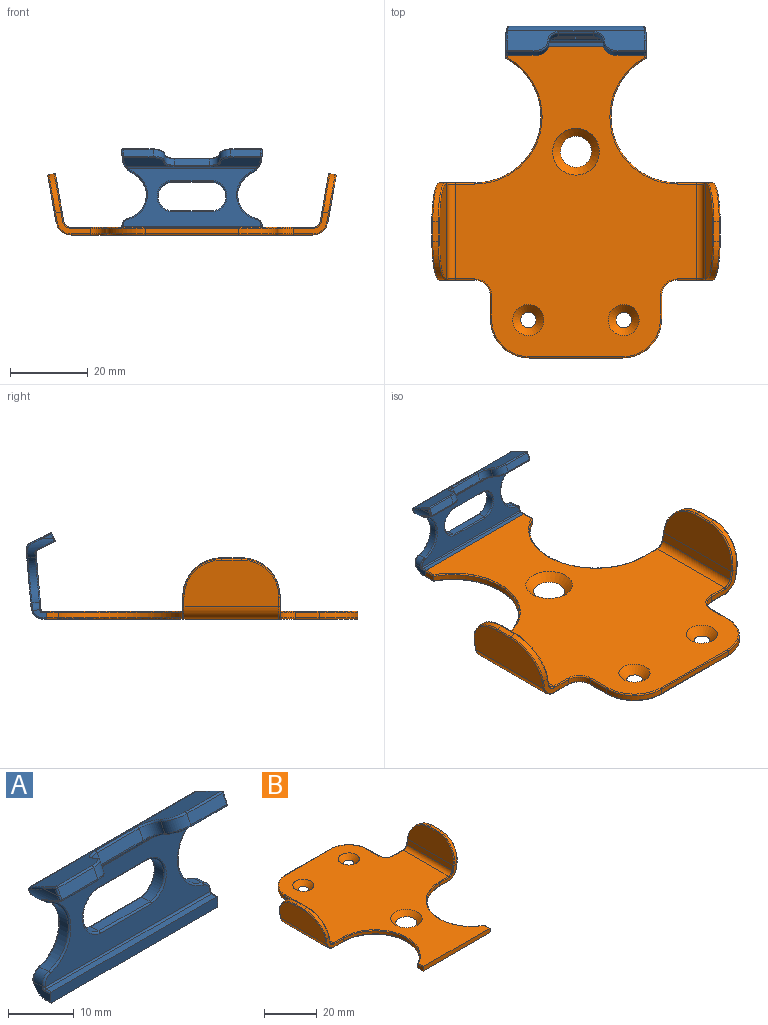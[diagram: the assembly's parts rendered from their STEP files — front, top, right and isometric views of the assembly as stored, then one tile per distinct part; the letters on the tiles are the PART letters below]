
ASSEMBLY  parts=2 mates=1
PART A: 99 faces, bbox 36.3x7.8x22.5 mm
  f0: plane 35.22x14.86mm, normal (0,1,-0.09), area 265.9mm2, adj f8,f15,f29,f30,f31,f32,f52,f53
  f1: plane 3.57x2.09mm, normal (1,0,0), area 4.9mm2, adj f6,f35,f46,f47,f48,f56,f57
  f2: plane 3.57x2.09mm, normal (-1,0,0), area 4.9mm2, adj f6,f36,f58,f59,f72,f73,f74
  f3: plane 11.89x4.49mm, normal (0,-0.45,-0.89), area 50.1mm2, adj f16,f41,f84,f86,f88
  f4: plane 35.4x5.1mm, normal (0,0.45,0.89), area 124.1mm2, adj f8,f49,f50,f65,f66,f87,f89,f91
  f5: plane 7.7x1.7mm, normal (0,-0.89,0.45), area 14.6mm2, adj f39,f77,f81,f83,f87
  f6: plane 36x2mm, normal (0,-1,0), area 71.9mm2, adj f1,f2,f7,f12,f48,f57,f58,f74
  f7: plane 35.4x0.98mm, normal (0,0,-1), area 34.8mm2, adj f6,f15,f57,f58
  f8: cylinder r=2mm len=35.17mm, axis (-1,0,0), area 82.8mm2, adj f0,f4,f51,f64
  f9: plane 7.7x1.7mm, normal (0,-0.89,0.45), area 14.6mm2, adj f40,f88,f92,f94,f98
  f10: plane 11.89x4.49mm, normal (0,-0.45,-0.89), area 50.1mm2, adj f16,f67,f75,f76,f77
  f11: plane 35.4x14.87mm, normal (0,-1,0.09), area 267.4mm2, adj f16,f17,f25,f26,f27,f28,f43,f44
  f12: plane 35.4x1.12mm, normal (0,0,1), area 39.7mm2, adj f6,f17,f48,f74
  f13: plane 3.08x1.29mm, normal (1,0,0), area 1.6mm2, adj f33,f49,f94
  f14: plane 3.08x1.29mm, normal (-1,0,0), area 1.6mm2, adj f34,f66,f83
  f15: cylinder r=3mm len=35.4mm, axis (-1,0,0), area 157.5mm2, adj f0,f7,f55,f56,f59,f60
  f16: cylinder r=0.5mm len=33.89mm, axis (1,0,0), area 17.9mm2, adj f3,f10,f11,f42,f68,f78,f80,f82
  f17: cylinder r=0.3mm len=35.4mm, axis (1,0,0), area 15.8mm2, adj f11,f12,f47,f73
  f18: plane 9x1.75mm, normal (0,-0.89,0.45), area 17.6mm2, adj f37,f38,f80,f93
  f19: cylinder r=6.25mm len=11.78mm, axis (0,1,-0.09), area 28.9mm2, adj f34,f36,f62,f70
  f20: cylinder r=6.25mm len=11.78mm, axis (0,1,-0.09), area 28.9mm2, adj f33,f35,f44,f53
  f21: plane 11x1.89mm, normal (0,-0.09,-1), area 20.9mm2, adj f22,f24,f28,f29
  f22: cylinder r=3.8mm len=7.64mm, axis (0,1,-0.09), area 20.3mm2, adj f21,f23,f27,f31
  f23: plane 11x1.89mm, normal (0,0.09,1), area 20.9mm2, adj f22,f24,f25,f32
  f24: cylinder r=3.8mm len=7.64mm, axis (0,1,-0.09), area 20.3mm2, adj f21,f23,f26,f30
  f25: cylinder r=0.3mm len=11.05mm, axis (-1,0,0), area 5.2mm2, adj f11,f23,f26,f27
  f26: torus R=4.1mm, axis (0,1,-0.09), area 5.2mm2, adj f11,f24,f25,f28
  f27: torus R=4.1mm, axis (0,1,-0.09), area 5.2mm2, adj f11,f22,f25,f28
  f28: cylinder r=0.3mm len=11.05mm, axis (1,0,0), area 5.2mm2, adj f11,f21,f26,f27
  f29: cylinder r=0.3mm len=11.05mm, axis (1,0,0), area 5.2mm2, adj f0,f21,f30,f31
  f30: torus R=4.1mm, axis (0,-1,0.09), area 5.2mm2, adj f0,f24,f29,f32
  f31: torus R=4.1mm, axis (0,-1,0.09), area 5.2mm2, adj f0,f22,f29,f32
  f32: cylinder r=0.3mm len=11.05mm, axis (-1,0,0), area 5.2mm2, adj f0,f23,f30,f31
  f33: cylinder r=5mm len=7.44mm, axis (0,1,-0.09), area 17.3mm2, adj f13,f20,f41,f42,f43,f50,f51,f52
  f34: cylinder r=5mm len=7.44mm, axis (0,1,-0.09), area 17.3mm2, adj f14,f19,f63,f64,f65,f67,f68,f69
  f35: cylinder r=2mm len=2.1mm, axis (0,1,-0.09), area 5mm2, adj f1,f20,f45,f54,f55
  f36: cylinder r=2mm len=2.1mm, axis (0,1,-0.09), area 5mm2, adj f2,f19,f60,f61,f71
  f37: cylinder r=2.5mm len=3.04mm, axis (0,0.45,0.89), area 7.3mm2, adj f18,f40,f82,f84,f95
  f38: cylinder r=2.5mm len=3.04mm, axis (0,-0.45,-0.89), area 7.3mm2, adj f18,f39,f76,f78,f91
  f39: cylinder r=3mm len=3.45mm, axis (0,-0.45,-0.89), area 8.8mm2, adj f5,f38,f75,f89
  f40: cylinder r=3mm len=3.45mm, axis (0,0.45,0.89), area 8.8mm2, adj f9,f37,f86,f97
  f41: bspline ~4.61x2.47mm, area 1.9mm2, adj f3,f33,f42,f90
  f42: bspline ~1.15x1.14mm, area 0.4mm2, adj f16,f33,f41,f43
  f43: torus R=4.7mm, axis (0,1,-0.09), area 0.8mm2, adj f11,f33,f42,f44
  f44: torus R=6.55mm, axis (0,1,-0.09), area 7.3mm2, adj f11,f20,f43,f45
  f45: torus R=1.7mm, axis (0,1,-0.09), area 1.2mm2, adj f11,f35,f44,f46
  f46: cylinder r=0.3mm len=0.31mm, axis (0,0.09,1), area 0.1mm2, adj f1,f11,f45,f47
  f47: torus R=0.6mm, axis (1,0,0), area 0.3mm2, adj f1,f17,f46,f48
  f48: cylinder r=0.3mm len=1.12mm, axis (0,1,0), area 0.5mm2, adj f1,f6,f12,f47
  f49: cylinder r=0.3mm len=2.71mm, axis (0,0.89,-0.45), area 1.4mm2, adj f4,f13,f50,f96
  f50: bspline ~4.11x2.33mm, area 1.4mm2, adj f4,f33,f49,f51
  f51: bspline ~2.43x1.6mm, area 1.3mm2, adj f8,f33,f50,f52
  f52: torus R=4.7mm, axis (0,-1,0.09), area 1.2mm2, adj f0,f33,f51,f53
  f53: torus R=6.55mm, axis (0,-1,0.09), area 7.3mm2, adj f0,f20,f52,f54
  f54: torus R=1.7mm, axis (0,-1,0.09), area 0.9mm2, adj f0,f35,f53,f55
  f55: bspline ~1.55x0.55mm, area 0.3mm2, adj f15,f35,f54,f56
  f56: torus R=2.7mm, axis (1,0,0), area 1.7mm2, adj f1,f15,f55,f57
  f57: cylinder r=0.3mm len=0.98mm, axis (0,-1,0), area 0.5mm2, adj f1,f6,f7,f56
  f58: cylinder r=0.3mm len=0.98mm, axis (0,1,0), area 0.5mm2, adj f2,f6,f7,f59
  f59: torus R=2.7mm, axis (1,0,0), area 1.7mm2, adj f2,f15,f58,f60
  f60: bspline ~1.55x0.55mm, area 0.3mm2, adj f15,f36,f59,f61
  f61: torus R=1.7mm, axis (0,-1,0.09), area 0.9mm2, adj f0,f36,f60,f62
  f62: torus R=6.55mm, axis (0,-1,0.09), area 7.3mm2, adj f0,f19,f61,f63
  f63: torus R=4.7mm, axis (0,-1,0.09), area 1.2mm2, adj f0,f34,f62,f64
  f64: bspline ~2.7x1.4mm, area 1.3mm2, adj f8,f34,f63,f65
  f65: bspline ~4.11x2.33mm, area 1.4mm2, adj f4,f34,f64,f66
  f66: cylinder r=0.3mm len=2.71mm, axis (0,-0.89,0.45), area 1.4mm2, adj f4,f14,f65,f85
  f67: bspline ~4.61x2.47mm, area 1.9mm2, adj f10,f34,f68,f79
  f68: bspline ~1.12x1.11mm, area 0.4mm2, adj f16,f34,f67,f69
  f69: torus R=4.7mm, axis (0,1,-0.09), area 0.8mm2, adj f11,f34,f68,f70
  f70: torus R=6.55mm, axis (0,1,-0.09), area 7.3mm2, adj f11,f19,f69,f71
  f71: torus R=1.7mm, axis (0,1,-0.09), area 1.2mm2, adj f11,f36,f70,f72
  f72: cylinder r=0.3mm len=0.31mm, axis (0,-0.09,-1), area 0.1mm2, adj f2,f11,f71,f73
  f73: torus R=0.6mm, axis (1,0,0), area 0.3mm2, adj f2,f17,f72,f74
  f74: cylinder r=0.3mm len=1.12mm, axis (0,-1,0), area 0.5mm2, adj f2,f6,f12,f73
  f75: torus R=2.7mm, axis (0,0.45,0.89), area 2.1mm2, adj f10,f39,f76,f77
  f76: torus R=2.8mm, axis (0,0.45,0.89), area 1.3mm2, adj f10,f38,f75,f78
  f77: cylinder r=0.3mm len=7.65mm, axis (-1,0,0), area 3.6mm2, adj f5,f10,f75,f79
  f78: bspline ~1.76x0.52mm, area 0.5mm2, adj f16,f38,f76,f80
  f79: sphere r=0.3mm, area 0.1mm2, adj f67,f77,f81
  f80: cylinder r=0.3mm len=9mm, axis (1,0,0), area 3.2mm2, adj f16,f18,f78,f82
  f81: bspline ~1.79x1.09mm, area 0.4mm2, adj f5,f34,f79,f83
  f82: bspline ~2.03x0.55mm, area 0.5mm2, adj f16,f37,f80,f84
  f83: cylinder r=0.3mm len=1.15mm, axis (0,-0.45,-0.89), area 0.5mm2, adj f5,f14,f81,f85
  f84: torus R=2.8mm, axis (0,0.45,0.89), area 1.3mm2, adj f3,f37,f82,f86
  f85: sphere r=0.3mm, area 0.1mm2, adj f66,f83,f87
  f86: torus R=2.7mm, axis (0,0.45,0.89), area 2.1mm2, adj f3,f40,f84,f88
  f87: cylinder r=0.3mm len=7.7mm, axis (-1,0,0), area 3.6mm2, adj f4,f5,f85,f89
  f88: cylinder r=0.3mm len=7.65mm, axis (-1,0,0), area 3.6mm2, adj f3,f9,f86,f90
  f89: torus R=2.7mm, axis (0,-0.45,-0.89), area 2.1mm2, adj f4,f39,f87,f91
  f90: sphere r=0.3mm, area 0.1mm2, adj f41,f88,f92
  f91: torus R=2.8mm, axis (0,-0.45,-0.89), area 1.9mm2, adj f4,f38,f89,f93
  f92: bspline ~1.79x1.09mm, area 0.4mm2, adj f9,f33,f90,f94
  f93: cylinder r=0.3mm len=9mm, axis (1,0,0), area 4.2mm2, adj f4,f18,f91,f95
  f94: cylinder r=0.3mm len=1.15mm, axis (0,0.45,0.89), area 0.5mm2, adj f9,f13,f92,f96
  f95: torus R=2.8mm, axis (0,-0.45,-0.89), area 1.9mm2, adj f4,f37,f93,f97
  f96: sphere r=0.3mm, area 0.1mm2, adj f49,f94,f98
  f97: torus R=2.7mm, axis (0,-0.45,-0.89), area 2.1mm2, adj f4,f40,f95,f98
  f98: cylinder r=0.3mm len=7.7mm, axis (-1,0,0), area 3.6mm2, adj f4,f9,f96,f97
PART B: 94 faces, bbox 74.4x80.9x17 mm
  f0: plane 24x1.4mm, normal (0,1,0), area 33.6mm2, adj f1,f15,f64,f82
  f1: cylinder r=10mm len=10mm, axis (0,0,-1), area 22mm2, adj f0,f2,f62,f80
  f2: plane 6x1.4mm, normal (-1,0,0), area 8.4mm2, adj f1,f3,f60,f78
  f3: cylinder r=4mm len=4mm, axis (0,0,-1), area 8.8mm2, adj f2,f4,f58,f76
  f4: plane 9.05x5.62mm, normal (0,1,0), area 16.2mm2, adj f3,f23,f52,f54,f56,f73,f74,f75
  f5: plane 9.05x5.62mm, normal (0,-1,0), area 16.2mm2, adj f6,f24,f40,f42,f44,f67,f68,f69
  f6: cylinder r=17mm len=32mm, axis (0,0,-1), area 63.1mm2, adj f5,f7,f38,f66
  f7: plane 3.06x1.76mm, normal (-1,0,0), area 5.1mm2, adj f6,f8,f17,f38,f65
  f8: plane 36x2mm, normal (0,-1,0), area 71.9mm2, adj f7,f9,f16,f17,f37,f65,f77
  f9: plane 3x1.4mm, normal (1,0,0), area 4.2mm2, adj f8,f10,f37,f77
  f10: cylinder r=17mm len=32mm, axis (0,0,-1), area 63.1mm2, adj f9,f11,f39,f79
  f11: plane 9.05x5.62mm, normal (0,-1,0), area 16.2mm2, adj f10,f32,f41,f43,f45,f81,f83,f85
  f12: plane 9.05x5.62mm, normal (0,1,0), area 16.2mm2, adj f13,f31,f53,f55,f57,f90,f92,f93
  f13: cylinder r=4mm len=4mm, axis (0,0,-1), area 8.8mm2, adj f12,f14,f59,f88
  f14: plane 6x1.4mm, normal (1,0,0), area 8.4mm2, adj f13,f15,f61,f86
  f15: cylinder r=10mm len=10mm, axis (0,0,-1), area 22mm2, adj f0,f14,f63,f84
  f16: plane 79.7x62mm, normal (0,0,1), area 3007mm2, adj f8,f18,f26,f34,f35,f36,f65,f66
  f17: plane 79.7x62mm, normal (0,0,-1), area 3146.1mm2, adj f7,f8,f21,f29,f34,f35,f36,f37
  f18: cylinder r=2mm len=24.4mm, axis (0,-1,0), area 68.1mm2, adj f16,f19,f68,f74
  f19: plane 24.4x2.32mm, normal (0.98,0,0.17), area 57.4mm2, adj f18,f25,f69,f73
  f20: plane 24.4x11.87mm, normal (-0.98,0,-0.17), area 253.7mm2, adj f21,f44,f46,f48,f50,f52
  f21: cylinder r=4mm len=24.4mm, axis (0,-1,0), area 136.3mm2, adj f17,f20,f42,f54
  f22: plane 5x1.38mm, normal (-0.17,0,0.98), area 7mm2, adj f23,f24,f48,f71
  f23: cylinder r=10mm len=10.09mm, axis (-0.98,0,-0.17), area 22mm2, adj f4,f22,f50,f72
  f24: cylinder r=10mm len=10.09mm, axis (-0.98,0,-0.17), area 22mm2, adj f5,f22,f46,f70
  f25: plane 24.4x9.55mm, normal (0.98,0,0.17), area 196.3mm2, adj f19,f70,f71,f72
  f26: cylinder r=2mm len=24.4mm, axis (0,-1,0), area 68.1mm2, adj f16,f27,f83,f92
  f27: plane 24.4x2.32mm, normal (-0.98,0,0.17), area 57.4mm2, adj f26,f33,f85,f93
  f28: plane 24.4x11.87mm, normal (0.98,0,-0.17), area 253.7mm2, adj f29,f45,f47,f49,f51,f53
  f29: cylinder r=4mm len=24.4mm, axis (0,-1,0), area 136.3mm2, adj f17,f28,f43,f55
  f30: plane 5x1.38mm, normal (0.17,0,0.98), area 7mm2, adj f31,f32,f49,f89
  f31: cylinder r=10mm len=10.09mm, axis (0.98,0,-0.17), area 22mm2, adj f12,f30,f51,f91
  f32: cylinder r=10mm len=10.09mm, axis (0.98,0,-0.17), area 22mm2, adj f11,f30,f47,f87
  f33: plane 24.4x9.55mm, normal (-0.98,0,0.17), area 196.3mm2, adj f27,f87,f89,f91
  f34: cone r=2mm half-angle=45deg, axis (0,0,1), area 53.3mm2, adj f16,f17
  f35: cone r=2mm half-angle=45deg, axis (0,0,1), area 53.3mm2, adj f16,f17
  f36: cone r=4mm half-angle=45deg, axis (0,0,1), area 88.9mm2, adj f16,f17
  f37: cylinder r=0.3mm len=3mm, axis (0,1,0), area 1.4mm2, adj f8,f9,f17,f39
  f38: torus R=17.3mm, axis (0,0,1), area 21.4mm2, adj f6,f7,f17,f40
  f39: torus R=17.3mm, axis (0,0,1), area 21.3mm2, adj f10,f17,f37,f41
  f40: cylinder r=0.3mm len=5mm, axis (1,0,0), area 2.4mm2, adj f5,f17,f38,f42
  f41: cylinder r=0.3mm len=5mm, axis (1,0,0), area 2.4mm2, adj f11,f17,f39,f43
  f42: torus R=3.7mm, axis (0,1,0), area 2.6mm2, adj f5,f21,f40,f44
  f43: torus R=3.7mm, axis (0,-1,0), area 2.6mm2, adj f11,f29,f41,f45
  f44: cylinder r=0.3mm len=2.37mm, axis (-0.17,0,0.98), area 1.1mm2, adj f5,f20,f42,f46
  f45: cylinder r=0.3mm len=2.37mm, axis (-0.17,0,-0.98), area 1.1mm2, adj f11,f28,f43,f47
  f46: torus R=9.7mm, axis (0.98,0,0.17), area 7.3mm2, adj f20,f24,f44,f48
  f47: torus R=9.7mm, axis (-0.98,0,0.17), area 7.3mm2, adj f28,f32,f45,f49
  f48: cylinder r=0.3mm len=5mm, axis (0,-1,0), area 2.4mm2, adj f20,f22,f46,f50
  f49: cylinder r=0.3mm len=5mm, axis (0,-1,0), area 2.4mm2, adj f28,f30,f47,f51
  f50: torus R=9.7mm, axis (0.98,0,0.17), area 7.3mm2, adj f20,f23,f48,f52
  f51: torus R=9.7mm, axis (-0.98,0,0.17), area 7.3mm2, adj f28,f31,f49,f53
  f52: cylinder r=0.3mm len=2.37mm, axis (-0.17,0,0.98), area 1.1mm2, adj f4,f20,f50,f54
  f53: cylinder r=0.3mm len=2.37mm, axis (-0.17,0,-0.98), area 1.1mm2, adj f12,f28,f51,f55
  f54: torus R=3.7mm, axis (0,-1,0), area 2.6mm2, adj f4,f21,f52,f56
  f55: torus R=3.7mm, axis (0,1,0), area 2.6mm2, adj f12,f29,f53,f57
  f56: cylinder r=0.3mm len=5mm, axis (-1,0,0), area 2.4mm2, adj f4,f17,f54,f58
  f57: cylinder r=0.3mm len=5mm, axis (-1,0,0), area 2.4mm2, adj f12,f17,f55,f59
  f58: torus R=4.3mm, axis (0,0,1), area 3mm2, adj f3,f17,f56,f60
  f59: torus R=4.3mm, axis (0,0,1), area 3mm2, adj f13,f17,f57,f61
  f60: cylinder r=0.3mm len=6mm, axis (0,-1,0), area 2.8mm2, adj f2,f17,f58,f62
  f61: cylinder r=0.3mm len=6mm, axis (0,1,0), area 2.8mm2, adj f14,f17,f59,f63
  f62: torus R=9.7mm, axis (0,0,1), area 7.3mm2, adj f1,f17,f60,f64
  f63: torus R=9.7mm, axis (0,0,1), area 7.3mm2, adj f15,f17,f61,f64
  f64: cylinder r=0.3mm len=24mm, axis (-1,0,0), area 11.3mm2, adj f0,f17,f62,f63
  f65: cylinder r=0.3mm len=3mm, axis (0,1,0), area 1.4mm2, adj f7,f8,f16,f66
  f66: torus R=17.3mm, axis (0,0,1), area 21.3mm2, adj f6,f16,f65,f67
  f67: cylinder r=0.3mm len=5mm, axis (-1,0,0), area 2.4mm2, adj f5,f16,f66,f68
  f68: torus R=2.3mm, axis (0,1,0), area 1.4mm2, adj f5,f18,f67,f69
  f69: cylinder r=0.3mm len=2.37mm, axis (0.17,0,-0.98), area 1.1mm2, adj f5,f19,f68,f70
  f70: torus R=9.7mm, axis (-0.98,0,-0.17), area 7.3mm2, adj f24,f25,f69,f71
  f71: cylinder r=0.3mm len=5mm, axis (0,-1,0), area 2.4mm2, adj f22,f25,f70,f72
  f72: torus R=9.7mm, axis (-0.98,0,-0.17), area 7.3mm2, adj f23,f25,f71,f73
  f73: cylinder r=0.3mm len=2.37mm, axis (0.17,0,-0.98), area 1.1mm2, adj f4,f19,f72,f74
  f74: torus R=2.3mm, axis (0,-1,0), area 1.4mm2, adj f4,f18,f73,f75
  f75: cylinder r=0.3mm len=5mm, axis (1,0,0), area 2.4mm2, adj f4,f16,f74,f76
  f76: torus R=4.3mm, axis (0,0,1), area 3mm2, adj f3,f16,f75,f78
  f77: cylinder r=0.3mm len=3mm, axis (0,-1,0), area 1.4mm2, adj f8,f9,f16,f79
  f78: cylinder r=0.3mm len=6mm, axis (0,1,0), area 2.8mm2, adj f2,f16,f76,f80
  f79: torus R=17.3mm, axis (0,0,1), area 21.3mm2, adj f10,f16,f77,f81
  f80: torus R=9.7mm, axis (0,0,1), area 7.3mm2, adj f1,f16,f78,f82
  f81: cylinder r=0.3mm len=5mm, axis (-1,0,0), area 2.4mm2, adj f11,f16,f79,f83
  f82: cylinder r=0.3mm len=24mm, axis (1,0,0), area 11.3mm2, adj f0,f16,f80,f84
  f83: torus R=2.3mm, axis (0,-1,0), area 1.4mm2, adj f11,f26,f81,f85
  f84: torus R=9.7mm, axis (0,0,1), area 7.3mm2, adj f15,f16,f82,f86
  f85: cylinder r=0.3mm len=2.37mm, axis (0.17,0,0.98), area 1.1mm2, adj f11,f27,f83,f87
  f86: cylinder r=0.3mm len=6mm, axis (0,-1,0), area 2.8mm2, adj f14,f16,f84,f88
  f87: torus R=9.7mm, axis (0.98,0,-0.17), area 7.3mm2, adj f32,f33,f85,f89
  f88: torus R=4.3mm, axis (0,0,1), area 3mm2, adj f13,f16,f86,f90
  f89: cylinder r=0.3mm len=5mm, axis (0,-1,0), area 2.4mm2, adj f30,f33,f87,f91
  f90: cylinder r=0.3mm len=5mm, axis (1,0,0), area 2.4mm2, adj f12,f16,f88,f92
  f91: torus R=9.7mm, axis (0.98,0,-0.17), area 7.3mm2, adj f31,f33,f89,f93
  f92: torus R=2.3mm, axis (0,1,0), area 1.4mm2, adj f12,f26,f90,f93
  f93: cylinder r=0.3mm len=2.37mm, axis (0.17,0,0.98), area 1.1mm2, adj f12,f27,f91,f92
PLACE A t=(-16.29,-23.57,-30.01)mm
PLACE B rot(axis=(0,0,1),180deg) t=(-16.29,-65.57,-30.01)mm
MATE fastened B.f8 <-> A.f6  axis (0,1,0) through (-16.29,-23.57,-29.01)mm
